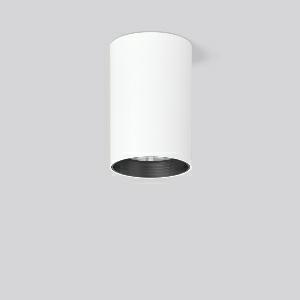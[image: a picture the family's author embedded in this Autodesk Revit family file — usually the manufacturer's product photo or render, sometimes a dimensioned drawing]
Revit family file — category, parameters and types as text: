
# Revit family: heledon_maxi_a_931229_002_3_76_9c8e
name_source: partatom
category: Lighting Fixtures
units: mm (PartAtom-declared; Revit-internal decimal feet)

## family parameters
Cut with Voids When Loaded = No
Host = Face
Light Source = No
Part Type = Normal
Room Calculation Point = No
Round Connector Dimension = Use Diameter
Shared = No

## types (1)
- HELEDON maxi A (1 x LED Modul 935, 3650 lm, 3500)
    Apparent Load = 35 VA
    Approval mark = CE
    CIE Flux Codes = 96 100 100 100 100
    Color Rendering = 92
    Color Temperature = 3500
    Default Elevation = 1800 mm
    Description = Series: HELEDON maxi
Cylindrical surface-mounted downlight. Housing: die-cast aluminium, powder-coated. Internal ceiling frame polycarbonate with bayonet mounting. Black plastic ring and recessed LED to prevent glare from the side. Optical assembly with lens made of plastic (polycarbonate) for the best homogeneous light distribution - can be changed without tools. Best colour rendering index Ra>90. Suitable for Ceiling mounting. Easy installation with a separate ceiling frame with bayonet mounting and plug connection. Driver integrated. Connected via plug-in connector. High quality converter without flickering and stroboscopic effect. The following accessories can be mounted without use of tools: interchangeable lenses, decorative glasses, honeycomb louvre, clear and frosted diffusers, white interchangeable plastic ring. 
Colour: traffic white, matt (RAL 9016)
Diameter: 123 mm
Height: 183 mm
Lamp: LED
Socket: without socket
Colour temperature: 3500K
Colour rendering index (CRI): 92
System power: 35 W
Rated luminous flux: 3650 lm
Luminous efficiency: 104 lm/W
Control gear: Converter, dimmable, DALI
Protection class: I
Type of protection: IP 20
    Height = 183 mm
    Lamp = 1 x LED Modul 935
    Lamp Light Flux = 3650 lm
    Lamp count = 1
    Length = 123 mm
    Lifetime = 50000 h
    Luminous efficacy = 104 lm/W
    Manufacturer = RZB
    ModVariant = No
    Model = 931229.002.3.76
    Mounting Place = Ceiling
    Mounting Type = Surface mounted
    Number of Poles = 1
    OnlyDefault = Yes
    Power Factor = 1
    Product Name = HELEDON maxi A
    Product group = Surface mounted downlights
    ProductGroupID = 302
    Protection Class = Protection class I
    Protection Degree = IP 20
    RLX_Detail_Level = 1
    RLX_Emergency_Light_Flux = 0 lm
    RLX_Emergency_Type = 0
    RLX_Emergency_Type_DB = No
    RlxData = <blob elided: 97009 chars, md5=995c0c57>
    Socket = socket
    Standby Power = 0 W
    System Light Flux = 3650 lm
    System Power = 35 W
    Type Comments = Product without accessories
    Type Image = 931193.002.jpg
    URL = http://relux.com
    VarID = ---
    Voltage = 230 V
    Voltage Range = 220-240 V
    Weight = 0.00 kg
    Width = 0 mm  [stored 0 ft]

note: [stored X ft] marks values corroborated as IEEE doubles in the binary element streams (Revit-internal decimal feet)

## geometry (parser evidence)
native form markers: Blend x4, Sweep x9
no freeform markers — native parametric forms only
